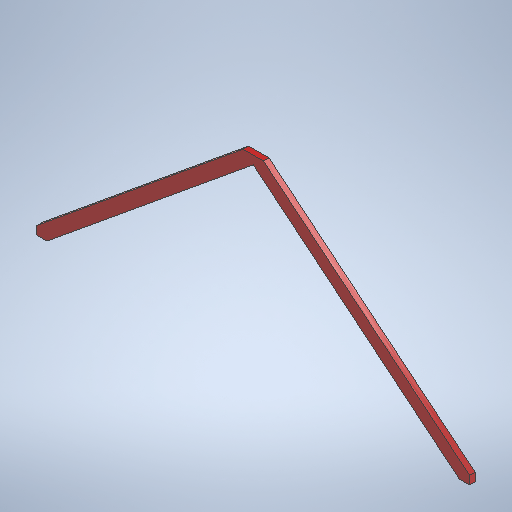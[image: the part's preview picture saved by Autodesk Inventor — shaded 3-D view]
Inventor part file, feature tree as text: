
AUTODESK INVENTOR PART (.ipt)
format: ipt  version: 2025.1 (Build 291241020, 241B)  size: 264,192 bytes
history: native  units: in
note: dims shown in document units (in); Inventor stores cm internally (conversion verified against a paired STEP export)
features: other x7, reference x4, extrude x1, sketch x1
ambient origin geometry x8: Origin, YZ Plane, XZ Plane, XY Plane, X Axis, Y Axis, Z Axis, Center Point
bodies: Solid1 (feature_tree)
feature tree (13):
  extrude  "Extrusion1"  [1 undecoded]
  sketch  "Sketch1"  dims[d4=1.5in d5=0.0in]
  reference  "Reference1"
  reference  "Reference2"
  reference  "Reference3"
  reference  "Reference4"
  other  "<userpath>\Documents\Tburn24\F_Legs1\B_Legs0.iam"
  other  "B_Legs0.iam"
  other  "8'x2x4:2"
  other  "4x2x4:2"
  other  "8'x2x4:4"
  other  "4x2x4:3"
  other  "Finish1"
note: 1 required parameter value undecoded (feature->parameter linkage not recoverable at this tier; creation-order binding heuristic only, values carry confidence <= 0.55)
